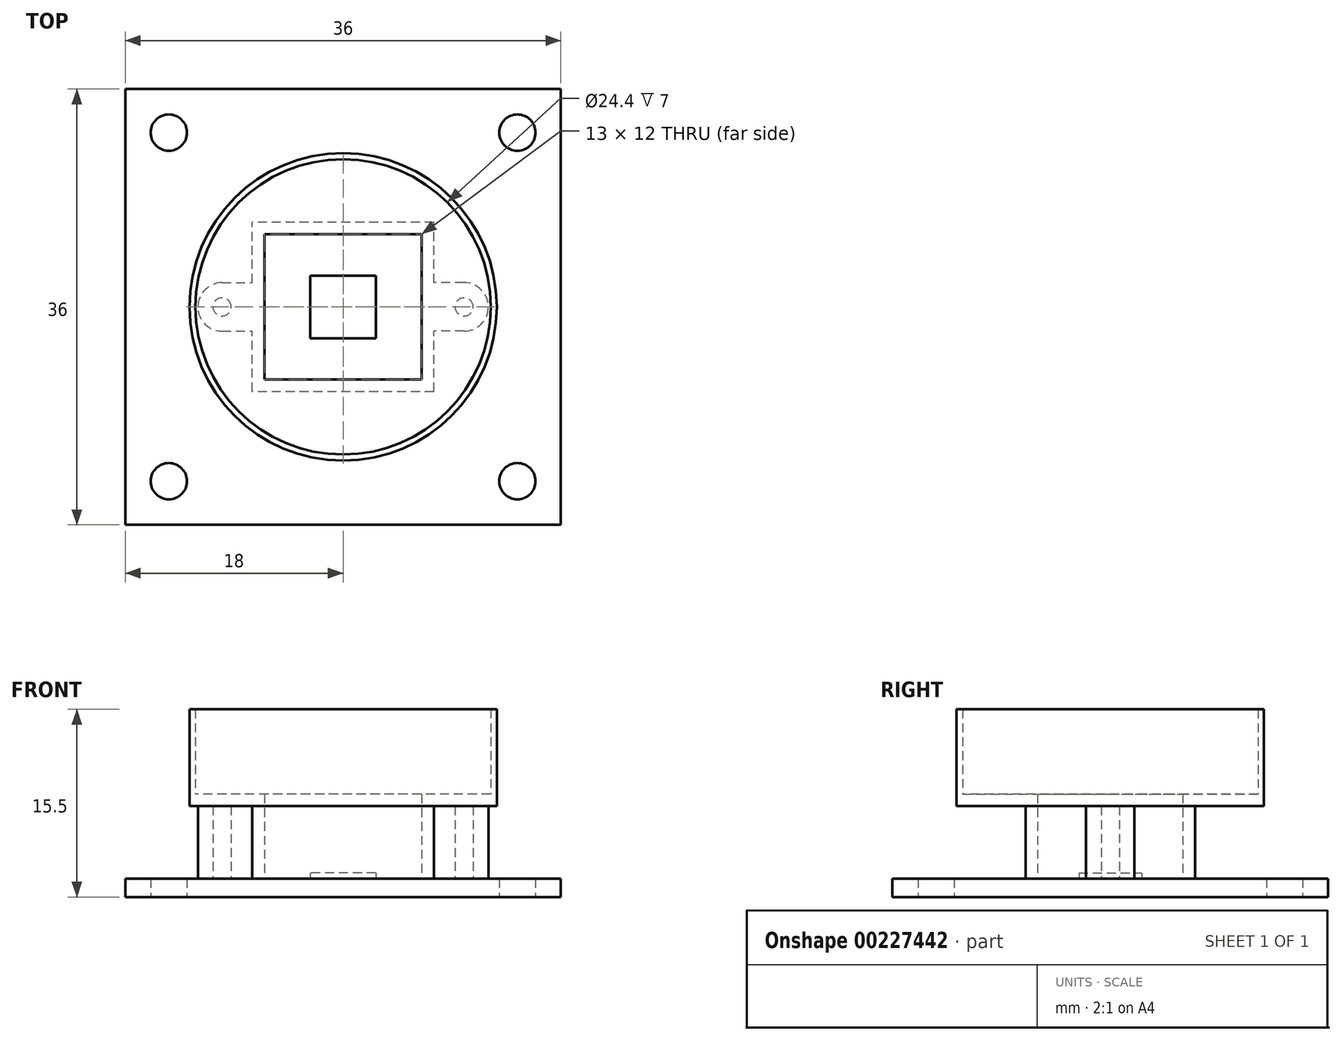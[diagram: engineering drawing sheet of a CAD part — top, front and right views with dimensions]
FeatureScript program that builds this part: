
annotation { "Feature Type Name" : "Feature", "Feature Type Description" : "" }
export const myFeature = defineFeature(function(context is Context, id is Id, definition is map)
    precondition{}
    {
        {
            var Q0;
            Q0=qCreatedBy(makeId("Top.planeOp"),FACE);
            var sketch = newSketch(context, id + "F0", { "sketchPlane" : qUnion([Q0])});
            skLineSegment(sketch, "E0.bottom", {"start": v(18, -18) * mm, "end": v(-18, -18) * mm});
            skLineSegment(sketch, "E0.top", {"start": v(18, 18) * mm, "end": v(-18, 18) * mm});
            skLineSegment(sketch, "E0.left", {"start": v(18, -18) * mm, "end": v(18, 18) * mm});
            skLineSegment(sketch, "E0.right", {"start": v(-18, -18) * mm, "end": v(-18, 18) * mm});
            skPoint(sketch, "E0.middle", {"position": v(0, 0) * mm});
            skPoint(sketch, "E1", {"position": v(-14.4, 14.4) * mm});
            skCircle(sketch, "E2", {"center": v(-14.4, 14.4) * mm, "radius": 1.5 * mm});
            skCircle(sketch, "E3.0.1.0", {"center": v(-14.4, -14.4) * mm, "radius": 1.5 * mm});
            skCircle(sketch, "E3.1.0.0", {"center": v(14.4, 14.4) * mm, "radius": 1.5 * mm});
            skCircle(sketch, "E3.1.1.0", {"center": v(14.4, -14.4) * mm, "radius": 1.5 * mm});
            skLineSegment(sketch, "E3.direction1", {"start": v(-14.4, 14.4) * mm, "end": v(14.4, 14.4) * mm, "construction": true});
            skLineSegment(sketch, "E3.direction2", {"start": v(-14.4, 14.4) * mm, "end": v(-14.4, -14.4) * mm, "construction": true});
            skSolve(sketch);
        }
        {
            var Q0;
            Q0=makeQuery(id+"F0.imprint","IMPRINT",FACE,{"disambiguationData":[TD([[makeQuery(id+"F0.imprint","IMPRINT",EDGE,{"derivedFrom":sQuery(id+"F0.wireOp",EDGE,"E0.bottom")}),-1.0]])]});
            extrude(context, id + "F1", {"entities" : qUnion([Q0]), "depth" : 1.5 * mm, "offsetDistance" : 25 * mm});
        }
        {
            var Q0;
            Q0=makeQuery(id+"F1.opExtrude","CAP_FACE",FACE,{"disambiguationData":[OSD([sQuery(id+"F0.wireOp",EDGE,"E0.bottom"),sQuery(id+"F0.wireOp",EDGE,"E0.top"),sQuery(id+"F0.wireOp",EDGE,"E0.left"),sQuery(id+"F0.wireOp",EDGE,"E0.right"),sQuery(id+"F0.wireOp",EDGE,"E2"),sQuery(id+"F0.wireOp",EDGE,"E3.0.1.0"),sQuery(id+"F0.wireOp",EDGE,"E3.1.0.0"),sQuery(id+"F0.wireOp",EDGE,"E3.1.1.0")])],"isStart":false});
            var sketch = newSketch(context, id + "F2", { "sketchPlane" : qUnion([Q0])});
            skLineSegment(sketch, "E4.bottom", {"start": v(2.7, -2.6) * mm, "end": v(-2.7, -2.6) * mm});
            skLineSegment(sketch, "E4.top", {"start": v(2.7, 2.6) * mm, "end": v(-2.7, 2.6) * mm});
            skLineSegment(sketch, "E4.left", {"start": v(2.7, -2.6) * mm, "end": v(2.7, 2.6) * mm});
            skLineSegment(sketch, "E4.right", {"start": v(-2.7, -2.6) * mm, "end": v(-2.7, 2.6) * mm});
            skPoint(sketch, "E4.middle", {"position": v(0, 0) * mm});
            skSolve(sketch);
        }
        {
            var Q0;
            Q0=makeQuery(id+"F2.imprint","IMPRINT",FACE,{"disambiguationData":[TD([[makeQuery(id+"F2.imprint","IMPRINT",EDGE,{"derivedFrom":sQuery(id+"F2.wireOp",EDGE,"E4.bottom")}),-1.0]])]});
            extrude(context, id + "F3", {"entities" : qUnion([Q0]), "depth" : 0.5 * mm});
        }
        {
            var Q0;
            Q0=makeQuery(id+"F1.opExtrude","CAP_FACE",FACE,{"disambiguationData":[OSD([sQuery(id+"F0.wireOp",EDGE,"E0.bottom"),sQuery(id+"F0.wireOp",EDGE,"E0.top"),sQuery(id+"F0.wireOp",EDGE,"E0.left"),sQuery(id+"F0.wireOp",EDGE,"E0.right"),sQuery(id+"F0.wireOp",EDGE,"E2"),sQuery(id+"F0.wireOp",EDGE,"E3.0.1.0"),sQuery(id+"F0.wireOp",EDGE,"E3.1.0.0"),sQuery(id+"F0.wireOp",EDGE,"E3.1.1.0")])],"isStart":false});
            var sketch = newSketch(context, id + "F4", { "sketchPlane" : qUnion([Q0])});
            skLineSegment(sketch, "E5.bottom", {"start": v(7.5, -7) * mm, "end": v(-7.5, -7) * mm});
            skLineSegment(sketch, "E5.top", {"start": v(7.5, 7) * mm, "end": v(-7.5, 7) * mm});
            skLineSegment(sketch, "E5.left", {"start": v(7.5, -7) * mm, "end": v(7.5, 7) * mm});
            skLineSegment(sketch, "E5.right", {"start": v(-7.5, -7) * mm, "end": v(-7.5, 7) * mm});
            skPoint(sketch, "E5.middle", {"position": v(0, 0) * mm});
            skPoint(sketch, "E6", {"position": v(10, 0) * mm});
            skCircle(sketch, "E7", {"center": v(10, 0) * mm, "radius": 0.75 * mm});
            skArc(sketch, "E8", {"start": v(10, -2) * mm, "mid": v(12, 0) * mm, "end": v(10, 2) * mm});
            skLineSegment(sketch, "E9", {"start": v(10, -2) * mm, "end": v(7.5, -2) * mm});
            skLineSegment(sketch, "E10", {"start": v(10, 2) * mm, "end": v(7.5, 2) * mm});
            skLineSegment(sketch, "E11.MirrorCS", {"start": v(-10, -2) * mm, "end": v(-7.5, -2) * mm});
            skArc(sketch, "E12.MirrorCS", {"start": v(-10, -2) * mm, "mid": v(-12, 0) * mm, "end": v(-10, 2) * mm});
            skLineSegment(sketch, "E13.MirrorCS", {"start": v(-10, 2) * mm, "end": v(-7.5, 2) * mm});
            skCircle(sketch, "E14.MirrorC", {"center": v(-10, 0) * mm, "radius": 0.75 * mm});
            skLineSegment(sketch, "E15.0", {"start": v(6.5, 6) * mm, "end": v(-6.5, 6) * mm});
            skLineSegment(sketch, "E15.1", {"start": v(6.5, -6) * mm, "end": v(6.5, 6) * mm});
            skLineSegment(sketch, "E15.2", {"start": v(6.5, -6) * mm, "end": v(-6.5, -6) * mm});
            skLineSegment(sketch, "E15.3", {"start": v(-6.5, -6) * mm, "end": v(-6.5, 6) * mm});
            skSolve(sketch);
        }
        {
            var Q0;
            {var subQ4=sQuery(id+"F4.wireOp",EDGE,"E5.bottom");Q0=makeQuery(id+"F4.imprint","IMPRINT",FACE,{"disambiguationData":[TD([[makeQuery(id+"F4.imprint","IMPRINT",EDGE,{"derivedFrom":subQ4}),-1.0]])]});}
            var Q1;
            {var subQ1=sQuery(id+"F4.wireOp",EDGE,"E11.MirrorCS");Q1=makeQuery(id+"F4.imprint","IMPRINT",FACE,{"disambiguationData":[TD([[makeQuery(id+"F4.imprint","IMPRINT",EDGE,{"derivedFrom":subQ1}),1.0]])]});}
            var Q2;
            Q2=makeQuery(id+"F4.imprint","IMPRINT",FACE,{"disambiguationData":[TD([[makeQuery(id+"F4.imprint","IMPRINT",EDGE,{"derivedFrom":sQuery(id+"F4.wireOp",EDGE,"E7")}),-1.0]])]});
            extrude(context, id + "F5", {"entities" : qUnion([Q0, Q1, Q2]), "depth" : 6 * mm});
        }
        {
            var Q0;
            Q0=makeQuery(id+"F5.opExtrude","CAP_FACE",FACE,{"disambiguationData":[OSD([sQuery(id+"F4.wireOp",EDGE,"E5.bottom"),sQuery(id+"F4.wireOp",EDGE,"E5.top"),sQuery(id+"F4.wireOp",EDGE,"E5.left"),sQuery(id+"F4.wireOp",EDGE,"E5.right"),sQuery(id+"F4.wireOp",EDGE,"E7"),sQuery(id+"F4.wireOp",EDGE,"E8"),sQuery(id+"F4.wireOp",EDGE,"E9"),sQuery(id+"F4.wireOp",EDGE,"E10"),sQuery(id+"F4.wireOp",EDGE,"E11.MirrorCS"),sQuery(id+"F4.wireOp",EDGE,"E12.MirrorCS"),sQuery(id+"F4.wireOp",EDGE,"E13.MirrorCS"),sQuery(id+"F4.wireOp",EDGE,"E14.MirrorC"),sQuery(id+"F4.wireOp",EDGE,"E15.0"),sQuery(id+"F4.wireOp",EDGE,"E15.1"),sQuery(id+"F4.wireOp",EDGE,"E15.2"),sQuery(id+"F4.wireOp",EDGE,"E15.3")])],"isStart":false});
            var sketch = newSketch(context, id + "F6", { "sketchPlane" : qUnion([Q0])});
            skCircle(sketch, "E16", {"center": v(0, 0) * mm, "radius": 12.7 * mm});
            skLineSegment(sketch, "E17.bottom", {"start": v(6.5, -6) * mm, "end": v(-6.5, -6) * mm});
            skLineSegment(sketch, "E17.top", {"start": v(6.5, 6) * mm, "end": v(-6.5, 6) * mm});
            skLineSegment(sketch, "E17.left", {"start": v(6.5, -6) * mm, "end": v(6.5, 6) * mm});
            skLineSegment(sketch, "E17.right", {"start": v(-6.5, -6) * mm, "end": v(-6.5, 6) * mm});
            skSolve(sketch);
        }
        {
            var Q0;
            Q0 = qSketchRegion(id + "F6", true);
            extrude(context, id + "F7", {"entities" : qUnion([Q0]), "operationType" : NewBodyOperationType.ADD, "depth" : 1 * mm});
        }
        {
            var Q0;
            Q0=makeQuery(id+"F7.opExtrude","CAP_FACE",FACE,{"disambiguationData":[OSD([sQuery(id+"F6.wireOp",EDGE,"E16"),sQuery(id+"F6.wireOp",EDGE,"E17.bottom"),sQuery(id+"F6.wireOp",EDGE,"E17.top"),sQuery(id+"F6.wireOp",EDGE,"E17.left"),sQuery(id+"F6.wireOp",EDGE,"E17.right")])],"isStart":false});
            var sketch = newSketch(context, id + "F8", { "sketchPlane" : qUnion([Q0])});
            skCircle(sketch, "E18.0", {"center": v(0, 0) * mm, "radius": 12.2 * mm});
            skSolve(sketch);
        }
        {
            var Q0;
            Q0=makeQuery(id+"F8.imprint","IMPRINT",FACE,{"disambiguationData":[TD([[makeQuery(id+"F8.imprint","IMPRINT",EDGE,{"derivedFrom":sQuery(id+"F8.wireOp",EDGE,"E18.0")}),-1.0]])]});
            extrude(context, id + "F9", {"entities" : qUnion([Q0]), "operationType" : NewBodyOperationType.ADD, "depth" : 7 * mm});
        }
    });
